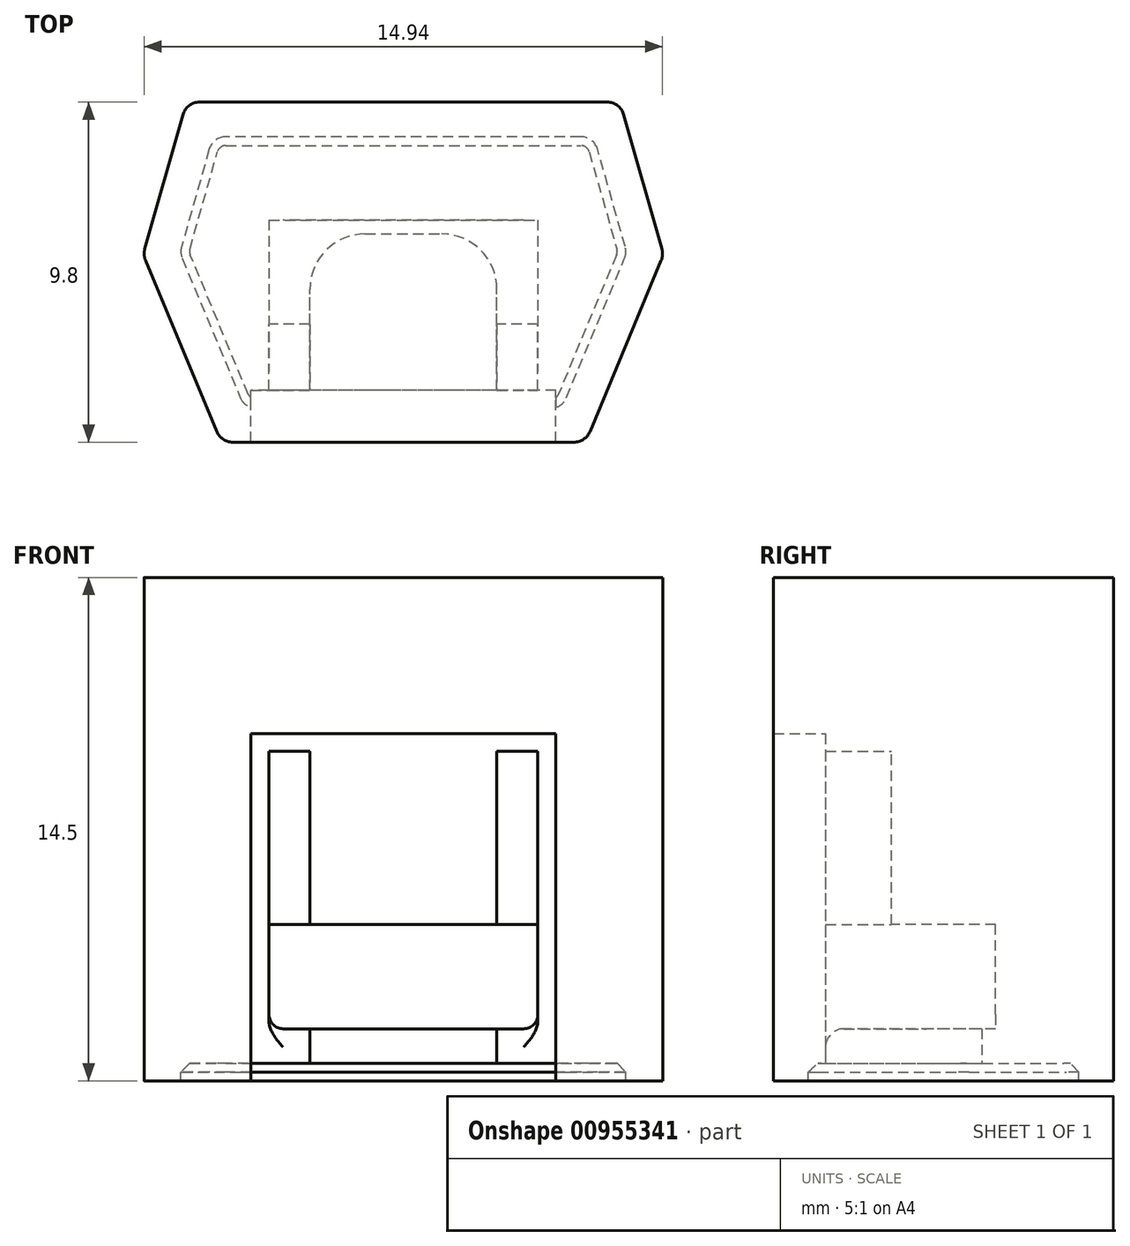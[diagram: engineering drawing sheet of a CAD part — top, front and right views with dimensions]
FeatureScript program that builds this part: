
annotation { "Feature Type Name" : "Feature", "Feature Type Description" : "" }
export const myFeature = defineFeature(function(context is Context, id is Id, definition is map)
    precondition{}
    {
        {
            var Q0;
            Q0=qCreatedBy(makeId("Top.planeOp"),FACE);
            var sketch = newSketch(context, id + "F0", { "sketchPlane" : qUnion([Q0])});
            skLineSegment(sketch, "E0", {"start": v(0, 4.4) * mm, "end": v(6.25, 4.4) * mm});
            skLineSegment(sketch, "E1", {"start": v(0, -5.4) * mm, "end": v(5.25, -5.4) * mm});
            skLineSegment(sketch, "E2", {"start": v(6.25, 4.4) * mm, "end": v(7.5, 0) * mm});
            skLineSegment(sketch, "E3", {"start": v(5.25, -5.4) * mm, "end": v(7.5, 0) * mm});
            skLineSegment(sketch, "E4.MirrorCS", {"start": v(0, -5.4) * mm, "end": v(-5.25, -5.4) * mm});
            skLineSegment(sketch, "E5.MirrorCS", {"start": v(-5.25, -5.4) * mm, "end": v(-7.5, 0) * mm});
            skLineSegment(sketch, "E6.MirrorCS", {"start": v(0, 4.4) * mm, "end": v(-6.25, 4.4) * mm});
            skLineSegment(sketch, "E7.MirrorCS", {"start": v(-6.25, 4.4) * mm, "end": v(-7.5, 0) * mm});
            skLineSegment(sketch, "E8", {"start": v(0, -5.4) * mm, "end": v(4.4, -5.4) * mm});
            skLineSegment(sketch, "E9", {"start": v(4.4, -5.4) * mm, "end": v(4.4, -3.9) * mm});
            skLineSegment(sketch, "E10", {"start": v(4.4, -3.9) * mm, "end": v(2.7, -3.9) * mm});
            skLineSegment(sketch, "E11", {"start": v(2.7, -3.9) * mm, "end": v(2.7, 0.6) * mm});
            skLineSegment(sketch, "E12", {"start": v(2.7, 0.6) * mm, "end": v(0, 0.6) * mm});
            skLineSegment(sketch, "E13.MirrorCS", {"start": v(-4.4, -5.4) * mm, "end": v(-4.4, -3.9) * mm});
            skLineSegment(sketch, "E14.MirrorCS", {"start": v(-4.4, -3.9) * mm, "end": v(-2.7, -3.9) * mm});
            skLineSegment(sketch, "E15.MirrorCS", {"start": v(-2.7, 0.6) * mm, "end": v(0, 0.6) * mm});
            skLineSegment(sketch, "E16.MirrorCS", {"start": v(-2.7, -3.9) * mm, "end": v(-2.7, 0.6) * mm});
            skSolve(sketch);
        }
        {
            var Q0;
            Q0=makeQuery(id+"F0.imprint","IMPRINT",FACE,{"disambiguationData":[TD([[makeQuery(id+"F0.imprint","IMPRINT",EDGE,{"derivedFrom":sQuery(id+"F0.wireOp",EDGE,"E0")}),-1.0]])]});
            extrude(context, id + "F1", {"entities" : qUnion([Q0]), "depth" : 14 * mm, "offsetDistance" : 25 * mm});
        }
        {
            var Q0;
            Q0=qCreatedBy(makeId("Front.planeOp"),FACE);
            var sketch = newSketch(context, id + "F2", { "sketchPlane" : qUnion([Q0])});
            skLineSegment(sketch, "E17", {"start": v(0, 0) * mm, "end": v(0, 1) * mm});
            skLineSegment(sketch, "E18", {"start": v(0, 1) * mm, "end": v(3.88, 1) * mm});
            skLineSegment(sketch, "E19", {"start": v(3.88, 1) * mm, "end": v(3.88, 9) * mm});
            skLineSegment(sketch, "E20", {"start": v(3.88, 9) * mm, "end": v(0, 9) * mm});
            skLineSegment(sketch, "E21", {"start": v(0, 4) * mm, "end": v(3.88, 4) * mm});
            skLineSegment(sketch, "E22.MirrorCS", {"start": v(-3.88, 9) * mm, "end": v(0, 9) * mm});
            skLineSegment(sketch, "E23.MirrorCS", {"start": v(0, 4) * mm, "end": v(-3.88, 4) * mm});
            skLineSegment(sketch, "E24.MirrorCS", {"start": v(0, 1) * mm, "end": v(-3.88, 1) * mm});
            skLineSegment(sketch, "E25.MirrorCS", {"start": v(-3.88, 1) * mm, "end": v(-3.88, 9) * mm});
            skSolve(sketch);
        }
        {
            var Q0;
            {var subQ2=sQuery(id+"F2.wireOp",EDGE,"E20");Q0=makeQuery(id+"F2.imprint","IMPRINT",FACE,{"disambiguationData":[TD([[makeQuery(id+"F2.imprint","IMPRINT",EDGE,{"derivedFrom":subQ2}),1.0]])]});}
            extrude(context, id + "F3", {"entities" : qUnion([Q0]), "operationType" : NewBodyOperationType.REMOVE, "depth" : 11.7 * mm, "offsetDistance" : 25 * mm, "hasSecondDirection" : true, "secondDirectionOppositeDirection" : false, "secondDirectionDepth" : 2 * mm});
        }
        {
            var Q0;
            {var subQ3=sQuery(id+"F2.wireOp",EDGE,"E18");Q0=makeQuery(id+"F2.imprint","IMPRINT",FACE,{"disambiguationData":[TD([[makeQuery(id+"F2.imprint","IMPRINT",EDGE,{"derivedFrom":subQ3}),1.0]])]});}
            extrude(context, id + "F4", {"entities" : qUnion([Q0]), "operationType" : NewBodyOperationType.REMOVE, "oppositeDirection" : true, "depth" : 1 * mm, "offsetDistance" : 25 * mm, "hasSecondDirection" : true, "secondDirectionOppositeDirection" : false, "secondDirectionDepth" : 22 * mm});
        }
        {
            var Q0;
            {var subQ0=sQuery(id+"F0.wireOp",EDGE,"E9");Q0=makeQuery(id+"F0.imprint","IMPRINT",FACE,{"disambiguationData":[TD([[makeQuery(id+"F0.imprint","IMPRINT",EDGE,{"derivedFrom":subQ0}),1.0]])]});}
            extrude(context, id + "F5", {"entities" : qUnion([Q0]), "operationType" : NewBodyOperationType.ADD, "depth" : 14 * mm, "offsetDistance" : 25 * mm, "hasSecondDirection" : true, "secondDirectionOppositeDirection" : false, "secondDirectionDepth" : 9.5 * mm});
        }
        {
            var Q0;
            {var subQ1=sQuery(id+"F0.wireOp",EDGE,"E15.MirrorCS");var subQ2=sQuery(id+"F0.wireOp",EDGE,"E12");Q0=makeQuery(id+"F4.boolean.opBoolean","SPLIT",FACE,{"disambiguationData":[TD([makeQuery(id+"F4.opExtrude","SWEPT_FACE",FACE,{"disambiguationData":[OSD([sQuery(id+"F2.wireOp",EDGE,"E21"),sQuery(id+"F2.wireOp",EDGE,"E23.MirrorCS")])]})])],"derivedFrom":makeQuery(id+"F1.opExtrude","SWEPT_FACE",FACE,{"disambiguationData":[OSD([subQ2,subQ1])]})});}
            extrude(context, id + "F6", {"entities" : qUnion([Q0]), "operationType" : NewBodyOperationType.ADD, "depth" : 4.5 * mm, "offsetDistance" : 25 * mm});
        }
        {
            var Q0;
            Q0=makeQuery(id+"F1.opExtrude","CAP_FACE",FACE,{"disambiguationData":[OSD([sQuery(id+"F0.wireOp",EDGE,"E0"),sQuery(id+"F0.wireOp",EDGE,"E1"),sQuery(id+"F0.wireOp",EDGE,"E2"),sQuery(id+"F0.wireOp",EDGE,"E3"),sQuery(id+"F0.wireOp",EDGE,"E4.MirrorCS"),sQuery(id+"F0.wireOp",EDGE,"E5.MirrorCS"),sQuery(id+"F0.wireOp",EDGE,"E6.MirrorCS"),sQuery(id+"F0.wireOp",EDGE,"E7.MirrorCS"),sQuery(id+"F0.wireOp",EDGE,"E9"),sQuery(id+"F0.wireOp",EDGE,"E10"),sQuery(id+"F0.wireOp",EDGE,"E11"),sQuery(id+"F0.wireOp",EDGE,"E12"),sQuery(id+"F0.wireOp",EDGE,"E13.MirrorCS"),sQuery(id+"F0.wireOp",EDGE,"E14.MirrorCS"),sQuery(id+"F0.wireOp",EDGE,"E15.MirrorCS"),sQuery(id+"F0.wireOp",EDGE,"E16.MirrorCS")])],"isStart":true});
            var sketch = newSketch(context, id + "F7", { "sketchPlane" : qUnion([Q0])});
            skLineSegment(sketch, "E26.0", {"start": v(4.4, 4.4) * mm, "end": v(4.58, 4.4) * mm});
            skLineSegment(sketch, "E26.1", {"start": v(4.58, 4.4) * mm, "end": v(6.44, -0.06) * mm});
            skLineSegment(sketch, "E26.2", {"start": v(5.5, -3.4) * mm, "end": v(6.44, -0.06) * mm});
            skLineSegment(sketch, "E26.3", {"start": v(-4.4, 4.4) * mm, "end": v(-4.58, 4.4) * mm});
            skLineSegment(sketch, "E26.4", {"start": v(-4.58, 4.4) * mm, "end": v(-6.44, -0.06) * mm});
            skLineSegment(sketch, "E26.5", {"start": v(-5.5, -3.4) * mm, "end": v(-6.44, -0.06) * mm});
            skLineSegment(sketch, "E26.6", {"start": v(-5.5, -3.4) * mm, "end": v(5.5, -3.4) * mm});
            skSolve(sketch);
        }
        {
            var Q0;
            {var subQ1=sQuery(id+"F7.wireOp",EDGE,"E26.0");Q0=makeQuery(id+"F7.imprint","IMPRINT",FACE,{"disambiguationData":[TD([[makeQuery(id+"F7.imprint","IMPRINT",EDGE,{"derivedFrom":subQ1}),1.0]])]});}
            extrude(context, id + "F8", {"entities" : qUnion([Q0]), "operationType" : NewBodyOperationType.ADD, "depth" : .5 * mm, "offsetDistance" : 25 * mm});
        }
        {
            var Q0;
            {var subQ1=sQuery(id+"F0.wireOp",EDGE,"E12");var subQ2=sQuery(id+"F0.wireOp",EDGE,"E11");Q0=makeQuery(id+"F4.boolean.opBoolean","SPLIT",EDGE,{"disambiguationData":[TD([makeQuery(id+"F4.opExtrude","SWEPT_FACE",FACE,{"disambiguationData":[OSD([sQuery(id+"F2.wireOp",EDGE,"E18"),sQuery(id+"F2.wireOp",EDGE,"E24.MirrorCS")])]})])],"derivedFrom":makeQuery(id+"F1.opExtrude","SWEPT_EDGE",EDGE,{"disambiguationData":[OSD([subQ2,subQ1])]})});}
            var Q1;
            {var subQ0=sQuery(id+"F0.wireOp",EDGE,"E16.MirrorCS");var subQ1=sQuery(id+"F0.wireOp",EDGE,"E15.MirrorCS");Q1=makeQuery(id+"F4.boolean.opBoolean","SPLIT",EDGE,{"disambiguationData":[TD([makeQuery(id+"F4.opExtrude","SWEPT_FACE",FACE,{"disambiguationData":[OSD([sQuery(id+"F2.wireOp",EDGE,"E18"),sQuery(id+"F2.wireOp",EDGE,"E24.MirrorCS")])]})])],"derivedFrom":makeQuery(id+"F1.opExtrude","SWEPT_EDGE",EDGE,{"disambiguationData":[OSD([subQ1,subQ0])]})});}
            fillet(context, id + "F9", {"entities" : qUnion([Q0, Q1]), "radius" : 1.6 * mm, "tangentPropagation" : true, "allowEdgeOverflow" : false});
        }
        {
            var Q0;
            Q0=makeQuery(id+"F4.boolean.opBoolean","INTERSECT",EDGE,{"derivedFrom":[makeQuery(id+"F1.opExtrude","SWEPT_FACE",FACE,{"disambiguationData":[OSD([sQuery(id+"F0.wireOp",EDGE,"E14.MirrorCS")])]}),makeQuery(id+"F4.opExtrude","SWEPT_FACE",FACE,{"disambiguationData":[OSD([sQuery(id+"F2.wireOp",EDGE,"E18"),sQuery(id+"F2.wireOp",EDGE,"E24.MirrorCS")])]})]});
            var Q1;
            Q1=makeQuery(id+"F4.boolean.opBoolean","INTERSECT",EDGE,{"derivedFrom":[makeQuery(id+"F1.opExtrude","SWEPT_FACE",FACE,{"disambiguationData":[OSD([sQuery(id+"F0.wireOp",EDGE,"E10")])]}),makeQuery(id+"F4.opExtrude","SWEPT_FACE",FACE,{"disambiguationData":[OSD([sQuery(id+"F2.wireOp",EDGE,"E18"),sQuery(id+"F2.wireOp",EDGE,"E24.MirrorCS")])]})]});
            fillet(context, id + "F10", {"entities" : qUnion([Q0, Q1]), "radius" : 0.53 * mm, "tangentPropagation" : true, "allowEdgeOverflow" : false});
        }
        {
            var Q0;
            Q0=makeQuery(id+"F4.boolean.opBoolean","COPY",EDGE,{"derivedFrom":makeQuery(id+"F4.opExtrude","SWEPT_EDGE",EDGE,{"disambiguationData":[OSD([sQuery(id+"F2.wireOp",EDGE,"E18"),sQuery(id+"F2.wireOp",EDGE,"E19")])]})});
            var Q1;
            Q1=makeQuery(id+"F4.boolean.opBoolean","COPY",EDGE,{"derivedFrom":makeQuery(id+"F4.opExtrude","SWEPT_EDGE",EDGE,{"disambiguationData":[OSD([sQuery(id+"F2.wireOp",EDGE,"E24.MirrorCS"),sQuery(id+"F2.wireOp",EDGE,"E25.MirrorCS")])]})});
            fillet(context, id + "F11", {"entities" : qUnion([Q0, Q1]), "radius" : 0.4 * mm, "tangentPropagation" : true, "allowEdgeOverflow" : false});
        }
        {
            var Q0;
            {var subQ0=sQuery(id+"F0.wireOp",EDGE,"E3");var subQ1=sQuery(id+"F0.wireOp",EDGE,"E1");Q0=makeQuery(id+"F8.boolean.opBoolean","MERGE",EDGE,{"derivedFrom":[makeQuery(id+"F1.opExtrude","SWEPT_EDGE",EDGE,{"disambiguationData":[OSD([subQ1,subQ0])]}),makeQuery(id+"F8.opExtrude","SWEPT_EDGE",EDGE,{"disambiguationData":[OSD([subQ1,subQ0])]})]});}
            var Q1;
            {var subQ0=sQuery(id+"F0.wireOp",EDGE,"E3");var subQ1=sQuery(id+"F0.wireOp",EDGE,"E2");Q1=makeQuery(id+"F8.boolean.opBoolean","MERGE",EDGE,{"derivedFrom":[makeQuery(id+"F1.opExtrude","SWEPT_EDGE",EDGE,{"disambiguationData":[OSD([subQ1,subQ0])]}),makeQuery(id+"F8.opExtrude","SWEPT_EDGE",EDGE,{"disambiguationData":[OSD([subQ1,subQ0])]})]});}
            var Q2;
            {var subQ0=sQuery(id+"F0.wireOp",EDGE,"E2");var subQ1=sQuery(id+"F0.wireOp",EDGE,"E0");Q2=makeQuery(id+"F8.boolean.opBoolean","MERGE",EDGE,{"derivedFrom":[makeQuery(id+"F1.opExtrude","SWEPT_EDGE",EDGE,{"disambiguationData":[OSD([subQ1,subQ0])]}),makeQuery(id+"F8.opExtrude","SWEPT_EDGE",EDGE,{"disambiguationData":[OSD([subQ1,subQ0,sQuery(id+"F0.wireOp",EDGE,"E6.MirrorCS")])]})]});}
            var Q3;
            {var subQ0=sQuery(id+"F0.wireOp",EDGE,"E7.MirrorCS");var subQ1=sQuery(id+"F0.wireOp",EDGE,"E6.MirrorCS");Q3=makeQuery(id+"F8.boolean.opBoolean","MERGE",EDGE,{"derivedFrom":[makeQuery(id+"F1.opExtrude","SWEPT_EDGE",EDGE,{"disambiguationData":[OSD([subQ1,subQ0])]}),makeQuery(id+"F8.opExtrude","SWEPT_EDGE",EDGE,{"disambiguationData":[OSD([sQuery(id+"F0.wireOp",EDGE,"E0"),subQ1,subQ0])]})]});}
            var Q4;
            {var subQ0=sQuery(id+"F0.wireOp",EDGE,"E7.MirrorCS");var subQ1=sQuery(id+"F0.wireOp",EDGE,"E5.MirrorCS");Q4=makeQuery(id+"F8.boolean.opBoolean","MERGE",EDGE,{"derivedFrom":[makeQuery(id+"F1.opExtrude","SWEPT_EDGE",EDGE,{"disambiguationData":[OSD([subQ1,subQ0])]}),makeQuery(id+"F8.opExtrude","SWEPT_EDGE",EDGE,{"disambiguationData":[OSD([subQ1,subQ0])]})]});}
            var Q5;
            {var subQ0=sQuery(id+"F0.wireOp",EDGE,"E5.MirrorCS");var subQ1=sQuery(id+"F0.wireOp",EDGE,"E4.MirrorCS");Q5=makeQuery(id+"F8.boolean.opBoolean","MERGE",EDGE,{"derivedFrom":[makeQuery(id+"F1.opExtrude","SWEPT_EDGE",EDGE,{"disambiguationData":[OSD([subQ1,subQ0])]}),makeQuery(id+"F8.opExtrude","SWEPT_EDGE",EDGE,{"disambiguationData":[OSD([subQ1,subQ0])]})]});}
            var Q6;
            Q6=makeQuery(id+"F8.opExtrude","SWEPT_EDGE",EDGE,{"disambiguationData":[OSD([sQuery(id+"F7.wireOp",EDGE,"E26.2"),sQuery(id+"F7.wireOp",EDGE,"E26.6")])]});
            var Q7;
            Q7=makeQuery(id+"F8.opExtrude","SWEPT_EDGE",EDGE,{"disambiguationData":[OSD([sQuery(id+"F7.wireOp",EDGE,"E26.1"),sQuery(id+"F7.wireOp",EDGE,"E26.2")])]});
            var Q8;
            Q8=makeQuery(id+"F8.opExtrude","SWEPT_EDGE",EDGE,{"disambiguationData":[OSD([sQuery(id+"F7.wireOp",EDGE,"E26.5"),sQuery(id+"F7.wireOp",EDGE,"E26.6")])]});
            var Q9;
            Q9=makeQuery(id+"F8.opExtrude","SWEPT_EDGE",EDGE,{"disambiguationData":[OSD([sQuery(id+"F7.wireOp",EDGE,"E26.4"),sQuery(id+"F7.wireOp",EDGE,"E26.5")])]});
            var Q10;
            Q10=makeQuery(id+"F8.opExtrude","SWEPT_EDGE",EDGE,{"disambiguationData":[OSD([sQuery(id+"F7.wireOp",EDGE,"E26.3"),sQuery(id+"F7.wireOp",EDGE,"E26.4")])]});
            var Q11;
            Q11=makeQuery(id+"F8.opExtrude","SWEPT_EDGE",EDGE,{"disambiguationData":[OSD([sQuery(id+"F7.wireOp",EDGE,"E26.0"),sQuery(id+"F7.wireOp",EDGE,"E26.1")])]});
            fillet(context, id + "F12", {"entities" : qUnion([Q0, Q1, Q2, Q3, Q4, Q5, Q6, Q7, Q8, Q9, Q10, Q11]), "radius" : 0.5 * mm, "tangentPropagation" : true, "allowEdgeOverflow" : false});
        }
        {
            var Q0;
            Q0=makeQuery(id+"F8.opExtrude","CAP_EDGE",EDGE,{"disambiguationData":[OSD([sQuery(id+"F7.wireOp",EDGE,"E26.5")])],"isStart":true});
            var Q1;
            Q1=makeQuery(id+"F12.opFillet","BLEND_EDGE",EDGE,{"blendedFrom":[makeQuery(id+"F8.opExtrude","SWEPT_EDGE",EDGE,{"disambiguationData":[OSD([sQuery(id+"F7.wireOp",EDGE,"E26.5"),sQuery(id+"F7.wireOp",EDGE,"E26.6")])]}),makeQuery(id+"F1.opExtrude","CAP_FACE",FACE,{"disambiguationData":[OSD([sQuery(id+"F0.wireOp",EDGE,"E0"),sQuery(id+"F0.wireOp",EDGE,"E1"),sQuery(id+"F0.wireOp",EDGE,"E2"),sQuery(id+"F0.wireOp",EDGE,"E3"),sQuery(id+"F0.wireOp",EDGE,"E4.MirrorCS"),sQuery(id+"F0.wireOp",EDGE,"E5.MirrorCS"),sQuery(id+"F0.wireOp",EDGE,"E6.MirrorCS"),sQuery(id+"F0.wireOp",EDGE,"E7.MirrorCS"),sQuery(id+"F0.wireOp",EDGE,"E9"),sQuery(id+"F0.wireOp",EDGE,"E10"),sQuery(id+"F0.wireOp",EDGE,"E11"),sQuery(id+"F0.wireOp",EDGE,"E12"),sQuery(id+"F0.wireOp",EDGE,"E13.MirrorCS"),sQuery(id+"F0.wireOp",EDGE,"E14.MirrorCS"),sQuery(id+"F0.wireOp",EDGE,"E15.MirrorCS"),sQuery(id+"F0.wireOp",EDGE,"E16.MirrorCS")])],"isStart":true})],"blendedInto":[makeQuery(id+"F1.opExtrude","CAP_FACE",FACE,{"disambiguationData":[OSD([sQuery(id+"F0.wireOp",EDGE,"E0"),sQuery(id+"F0.wireOp",EDGE,"E1"),sQuery(id+"F0.wireOp",EDGE,"E2"),sQuery(id+"F0.wireOp",EDGE,"E3"),sQuery(id+"F0.wireOp",EDGE,"E4.MirrorCS"),sQuery(id+"F0.wireOp",EDGE,"E5.MirrorCS"),sQuery(id+"F0.wireOp",EDGE,"E6.MirrorCS"),sQuery(id+"F0.wireOp",EDGE,"E7.MirrorCS"),sQuery(id+"F0.wireOp",EDGE,"E9"),sQuery(id+"F0.wireOp",EDGE,"E10"),sQuery(id+"F0.wireOp",EDGE,"E11"),sQuery(id+"F0.wireOp",EDGE,"E12"),sQuery(id+"F0.wireOp",EDGE,"E13.MirrorCS"),sQuery(id+"F0.wireOp",EDGE,"E14.MirrorCS"),sQuery(id+"F0.wireOp",EDGE,"E15.MirrorCS"),sQuery(id+"F0.wireOp",EDGE,"E16.MirrorCS")])],"isStart":true})]});
            var Q2;
            Q2=makeQuery(id+"F12.opFillet","BLEND_EDGE",EDGE,{"blendedFrom":[makeQuery(id+"F8.opExtrude","SWEPT_EDGE",EDGE,{"disambiguationData":[OSD([sQuery(id+"F7.wireOp",EDGE,"E26.4"),sQuery(id+"F7.wireOp",EDGE,"E26.5")])]}),makeQuery(id+"F1.opExtrude","CAP_FACE",FACE,{"disambiguationData":[OSD([sQuery(id+"F0.wireOp",EDGE,"E0"),sQuery(id+"F0.wireOp",EDGE,"E1"),sQuery(id+"F0.wireOp",EDGE,"E2"),sQuery(id+"F0.wireOp",EDGE,"E3"),sQuery(id+"F0.wireOp",EDGE,"E4.MirrorCS"),sQuery(id+"F0.wireOp",EDGE,"E5.MirrorCS"),sQuery(id+"F0.wireOp",EDGE,"E6.MirrorCS"),sQuery(id+"F0.wireOp",EDGE,"E7.MirrorCS"),sQuery(id+"F0.wireOp",EDGE,"E9"),sQuery(id+"F0.wireOp",EDGE,"E10"),sQuery(id+"F0.wireOp",EDGE,"E11"),sQuery(id+"F0.wireOp",EDGE,"E12"),sQuery(id+"F0.wireOp",EDGE,"E13.MirrorCS"),sQuery(id+"F0.wireOp",EDGE,"E14.MirrorCS"),sQuery(id+"F0.wireOp",EDGE,"E15.MirrorCS"),sQuery(id+"F0.wireOp",EDGE,"E16.MirrorCS")])],"isStart":true})],"blendedInto":[makeQuery(id+"F1.opExtrude","CAP_FACE",FACE,{"disambiguationData":[OSD([sQuery(id+"F0.wireOp",EDGE,"E0"),sQuery(id+"F0.wireOp",EDGE,"E1"),sQuery(id+"F0.wireOp",EDGE,"E2"),sQuery(id+"F0.wireOp",EDGE,"E3"),sQuery(id+"F0.wireOp",EDGE,"E4.MirrorCS"),sQuery(id+"F0.wireOp",EDGE,"E5.MirrorCS"),sQuery(id+"F0.wireOp",EDGE,"E6.MirrorCS"),sQuery(id+"F0.wireOp",EDGE,"E7.MirrorCS"),sQuery(id+"F0.wireOp",EDGE,"E9"),sQuery(id+"F0.wireOp",EDGE,"E10"),sQuery(id+"F0.wireOp",EDGE,"E11"),sQuery(id+"F0.wireOp",EDGE,"E12"),sQuery(id+"F0.wireOp",EDGE,"E13.MirrorCS"),sQuery(id+"F0.wireOp",EDGE,"E14.MirrorCS"),sQuery(id+"F0.wireOp",EDGE,"E15.MirrorCS"),sQuery(id+"F0.wireOp",EDGE,"E16.MirrorCS")])],"isStart":true})]});
            var Q3;
            Q3=makeQuery(id+"F8.opExtrude","CAP_EDGE",EDGE,{"disambiguationData":[OSD([sQuery(id+"F7.wireOp",EDGE,"E26.4")])],"isStart":true});
            var Q4;
            Q4=makeQuery(id+"F12.opFillet","BLEND_EDGE",EDGE,{"blendedFrom":[makeQuery(id+"F8.opExtrude","SWEPT_EDGE",EDGE,{"disambiguationData":[OSD([sQuery(id+"F7.wireOp",EDGE,"E26.3"),sQuery(id+"F7.wireOp",EDGE,"E26.4")])]}),makeQuery(id+"F1.opExtrude","CAP_FACE",FACE,{"disambiguationData":[OSD([sQuery(id+"F0.wireOp",EDGE,"E0"),sQuery(id+"F0.wireOp",EDGE,"E1"),sQuery(id+"F0.wireOp",EDGE,"E2"),sQuery(id+"F0.wireOp",EDGE,"E3"),sQuery(id+"F0.wireOp",EDGE,"E4.MirrorCS"),sQuery(id+"F0.wireOp",EDGE,"E5.MirrorCS"),sQuery(id+"F0.wireOp",EDGE,"E6.MirrorCS"),sQuery(id+"F0.wireOp",EDGE,"E7.MirrorCS"),sQuery(id+"F0.wireOp",EDGE,"E9"),sQuery(id+"F0.wireOp",EDGE,"E10"),sQuery(id+"F0.wireOp",EDGE,"E11"),sQuery(id+"F0.wireOp",EDGE,"E12"),sQuery(id+"F0.wireOp",EDGE,"E13.MirrorCS"),sQuery(id+"F0.wireOp",EDGE,"E14.MirrorCS"),sQuery(id+"F0.wireOp",EDGE,"E15.MirrorCS"),sQuery(id+"F0.wireOp",EDGE,"E16.MirrorCS")])],"isStart":true})],"blendedInto":[makeQuery(id+"F1.opExtrude","CAP_FACE",FACE,{"disambiguationData":[OSD([sQuery(id+"F0.wireOp",EDGE,"E0"),sQuery(id+"F0.wireOp",EDGE,"E1"),sQuery(id+"F0.wireOp",EDGE,"E2"),sQuery(id+"F0.wireOp",EDGE,"E3"),sQuery(id+"F0.wireOp",EDGE,"E4.MirrorCS"),sQuery(id+"F0.wireOp",EDGE,"E5.MirrorCS"),sQuery(id+"F0.wireOp",EDGE,"E6.MirrorCS"),sQuery(id+"F0.wireOp",EDGE,"E7.MirrorCS"),sQuery(id+"F0.wireOp",EDGE,"E9"),sQuery(id+"F0.wireOp",EDGE,"E10"),sQuery(id+"F0.wireOp",EDGE,"E11"),sQuery(id+"F0.wireOp",EDGE,"E12"),sQuery(id+"F0.wireOp",EDGE,"E13.MirrorCS"),sQuery(id+"F0.wireOp",EDGE,"E14.MirrorCS"),sQuery(id+"F0.wireOp",EDGE,"E15.MirrorCS"),sQuery(id+"F0.wireOp",EDGE,"E16.MirrorCS")])],"isStart":true})]});
            var Q5;
            Q5=makeQuery(id+"F12.opFillet","BLEND_EDGE",EDGE,{"blendedFrom":[makeQuery(id+"F8.opExtrude","SWEPT_EDGE",EDGE,{"disambiguationData":[OSD([sQuery(id+"F7.wireOp",EDGE,"E26.0"),sQuery(id+"F7.wireOp",EDGE,"E26.1")])]}),makeQuery(id+"F1.opExtrude","CAP_FACE",FACE,{"disambiguationData":[OSD([sQuery(id+"F0.wireOp",EDGE,"E0"),sQuery(id+"F0.wireOp",EDGE,"E1"),sQuery(id+"F0.wireOp",EDGE,"E2"),sQuery(id+"F0.wireOp",EDGE,"E3"),sQuery(id+"F0.wireOp",EDGE,"E4.MirrorCS"),sQuery(id+"F0.wireOp",EDGE,"E5.MirrorCS"),sQuery(id+"F0.wireOp",EDGE,"E6.MirrorCS"),sQuery(id+"F0.wireOp",EDGE,"E7.MirrorCS"),sQuery(id+"F0.wireOp",EDGE,"E9"),sQuery(id+"F0.wireOp",EDGE,"E10"),sQuery(id+"F0.wireOp",EDGE,"E11"),sQuery(id+"F0.wireOp",EDGE,"E12"),sQuery(id+"F0.wireOp",EDGE,"E13.MirrorCS"),sQuery(id+"F0.wireOp",EDGE,"E14.MirrorCS"),sQuery(id+"F0.wireOp",EDGE,"E15.MirrorCS"),sQuery(id+"F0.wireOp",EDGE,"E16.MirrorCS")])],"isStart":true})],"blendedInto":[makeQuery(id+"F1.opExtrude","CAP_FACE",FACE,{"disambiguationData":[OSD([sQuery(id+"F0.wireOp",EDGE,"E0"),sQuery(id+"F0.wireOp",EDGE,"E1"),sQuery(id+"F0.wireOp",EDGE,"E2"),sQuery(id+"F0.wireOp",EDGE,"E3"),sQuery(id+"F0.wireOp",EDGE,"E4.MirrorCS"),sQuery(id+"F0.wireOp",EDGE,"E5.MirrorCS"),sQuery(id+"F0.wireOp",EDGE,"E6.MirrorCS"),sQuery(id+"F0.wireOp",EDGE,"E7.MirrorCS"),sQuery(id+"F0.wireOp",EDGE,"E9"),sQuery(id+"F0.wireOp",EDGE,"E10"),sQuery(id+"F0.wireOp",EDGE,"E11"),sQuery(id+"F0.wireOp",EDGE,"E12"),sQuery(id+"F0.wireOp",EDGE,"E13.MirrorCS"),sQuery(id+"F0.wireOp",EDGE,"E14.MirrorCS"),sQuery(id+"F0.wireOp",EDGE,"E15.MirrorCS"),sQuery(id+"F0.wireOp",EDGE,"E16.MirrorCS")])],"isStart":true})]});
            var Q6;
            Q6=makeQuery(id+"F8.opExtrude","CAP_EDGE",EDGE,{"disambiguationData":[OSD([sQuery(id+"F7.wireOp",EDGE,"E26.1")])],"isStart":true});
            var Q7;
            Q7=makeQuery(id+"F12.opFillet","BLEND_EDGE",EDGE,{"blendedFrom":[makeQuery(id+"F8.opExtrude","SWEPT_EDGE",EDGE,{"disambiguationData":[OSD([sQuery(id+"F7.wireOp",EDGE,"E26.1"),sQuery(id+"F7.wireOp",EDGE,"E26.2")])]}),makeQuery(id+"F1.opExtrude","CAP_FACE",FACE,{"disambiguationData":[OSD([sQuery(id+"F0.wireOp",EDGE,"E0"),sQuery(id+"F0.wireOp",EDGE,"E1"),sQuery(id+"F0.wireOp",EDGE,"E2"),sQuery(id+"F0.wireOp",EDGE,"E3"),sQuery(id+"F0.wireOp",EDGE,"E4.MirrorCS"),sQuery(id+"F0.wireOp",EDGE,"E5.MirrorCS"),sQuery(id+"F0.wireOp",EDGE,"E6.MirrorCS"),sQuery(id+"F0.wireOp",EDGE,"E7.MirrorCS"),sQuery(id+"F0.wireOp",EDGE,"E9"),sQuery(id+"F0.wireOp",EDGE,"E10"),sQuery(id+"F0.wireOp",EDGE,"E11"),sQuery(id+"F0.wireOp",EDGE,"E12"),sQuery(id+"F0.wireOp",EDGE,"E13.MirrorCS"),sQuery(id+"F0.wireOp",EDGE,"E14.MirrorCS"),sQuery(id+"F0.wireOp",EDGE,"E15.MirrorCS"),sQuery(id+"F0.wireOp",EDGE,"E16.MirrorCS")])],"isStart":true})],"blendedInto":[makeQuery(id+"F1.opExtrude","CAP_FACE",FACE,{"disambiguationData":[OSD([sQuery(id+"F0.wireOp",EDGE,"E0"),sQuery(id+"F0.wireOp",EDGE,"E1"),sQuery(id+"F0.wireOp",EDGE,"E2"),sQuery(id+"F0.wireOp",EDGE,"E3"),sQuery(id+"F0.wireOp",EDGE,"E4.MirrorCS"),sQuery(id+"F0.wireOp",EDGE,"E5.MirrorCS"),sQuery(id+"F0.wireOp",EDGE,"E6.MirrorCS"),sQuery(id+"F0.wireOp",EDGE,"E7.MirrorCS"),sQuery(id+"F0.wireOp",EDGE,"E9"),sQuery(id+"F0.wireOp",EDGE,"E10"),sQuery(id+"F0.wireOp",EDGE,"E11"),sQuery(id+"F0.wireOp",EDGE,"E12"),sQuery(id+"F0.wireOp",EDGE,"E13.MirrorCS"),sQuery(id+"F0.wireOp",EDGE,"E14.MirrorCS"),sQuery(id+"F0.wireOp",EDGE,"E15.MirrorCS"),sQuery(id+"F0.wireOp",EDGE,"E16.MirrorCS")])],"isStart":true})]});
            var Q8;
            Q8=makeQuery(id+"F8.opExtrude","CAP_EDGE",EDGE,{"disambiguationData":[OSD([sQuery(id+"F7.wireOp",EDGE,"E26.2")])],"isStart":true});
            var Q9;
            Q9=makeQuery(id+"F12.opFillet","BLEND_EDGE",EDGE,{"blendedFrom":[makeQuery(id+"F8.opExtrude","SWEPT_EDGE",EDGE,{"disambiguationData":[OSD([sQuery(id+"F7.wireOp",EDGE,"E26.2"),sQuery(id+"F7.wireOp",EDGE,"E26.6")])]}),makeQuery(id+"F1.opExtrude","CAP_FACE",FACE,{"disambiguationData":[OSD([sQuery(id+"F0.wireOp",EDGE,"E0"),sQuery(id+"F0.wireOp",EDGE,"E1"),sQuery(id+"F0.wireOp",EDGE,"E2"),sQuery(id+"F0.wireOp",EDGE,"E3"),sQuery(id+"F0.wireOp",EDGE,"E4.MirrorCS"),sQuery(id+"F0.wireOp",EDGE,"E5.MirrorCS"),sQuery(id+"F0.wireOp",EDGE,"E6.MirrorCS"),sQuery(id+"F0.wireOp",EDGE,"E7.MirrorCS"),sQuery(id+"F0.wireOp",EDGE,"E9"),sQuery(id+"F0.wireOp",EDGE,"E10"),sQuery(id+"F0.wireOp",EDGE,"E11"),sQuery(id+"F0.wireOp",EDGE,"E12"),sQuery(id+"F0.wireOp",EDGE,"E13.MirrorCS"),sQuery(id+"F0.wireOp",EDGE,"E14.MirrorCS"),sQuery(id+"F0.wireOp",EDGE,"E15.MirrorCS"),sQuery(id+"F0.wireOp",EDGE,"E16.MirrorCS")])],"isStart":true})],"blendedInto":[makeQuery(id+"F1.opExtrude","CAP_FACE",FACE,{"disambiguationData":[OSD([sQuery(id+"F0.wireOp",EDGE,"E0"),sQuery(id+"F0.wireOp",EDGE,"E1"),sQuery(id+"F0.wireOp",EDGE,"E2"),sQuery(id+"F0.wireOp",EDGE,"E3"),sQuery(id+"F0.wireOp",EDGE,"E4.MirrorCS"),sQuery(id+"F0.wireOp",EDGE,"E5.MirrorCS"),sQuery(id+"F0.wireOp",EDGE,"E6.MirrorCS"),sQuery(id+"F0.wireOp",EDGE,"E7.MirrorCS"),sQuery(id+"F0.wireOp",EDGE,"E9"),sQuery(id+"F0.wireOp",EDGE,"E10"),sQuery(id+"F0.wireOp",EDGE,"E11"),sQuery(id+"F0.wireOp",EDGE,"E12"),sQuery(id+"F0.wireOp",EDGE,"E13.MirrorCS"),sQuery(id+"F0.wireOp",EDGE,"E14.MirrorCS"),sQuery(id+"F0.wireOp",EDGE,"E15.MirrorCS"),sQuery(id+"F0.wireOp",EDGE,"E16.MirrorCS")])],"isStart":true})]});
            var Q10;
            Q10=makeQuery(id+"F8.opExtrude","CAP_EDGE",EDGE,{"disambiguationData":[OSD([sQuery(id+"F7.wireOp",EDGE,"E26.6")])],"isStart":true});
            chamfer(context, id + "F13", {"entities" : qUnion([Q0, Q1, Q2, Q3, Q4, Q5, Q6, Q7, Q8, Q9, Q10]), "width" : .25 * mm, "tangentPropagation" : true});
        }
    });
